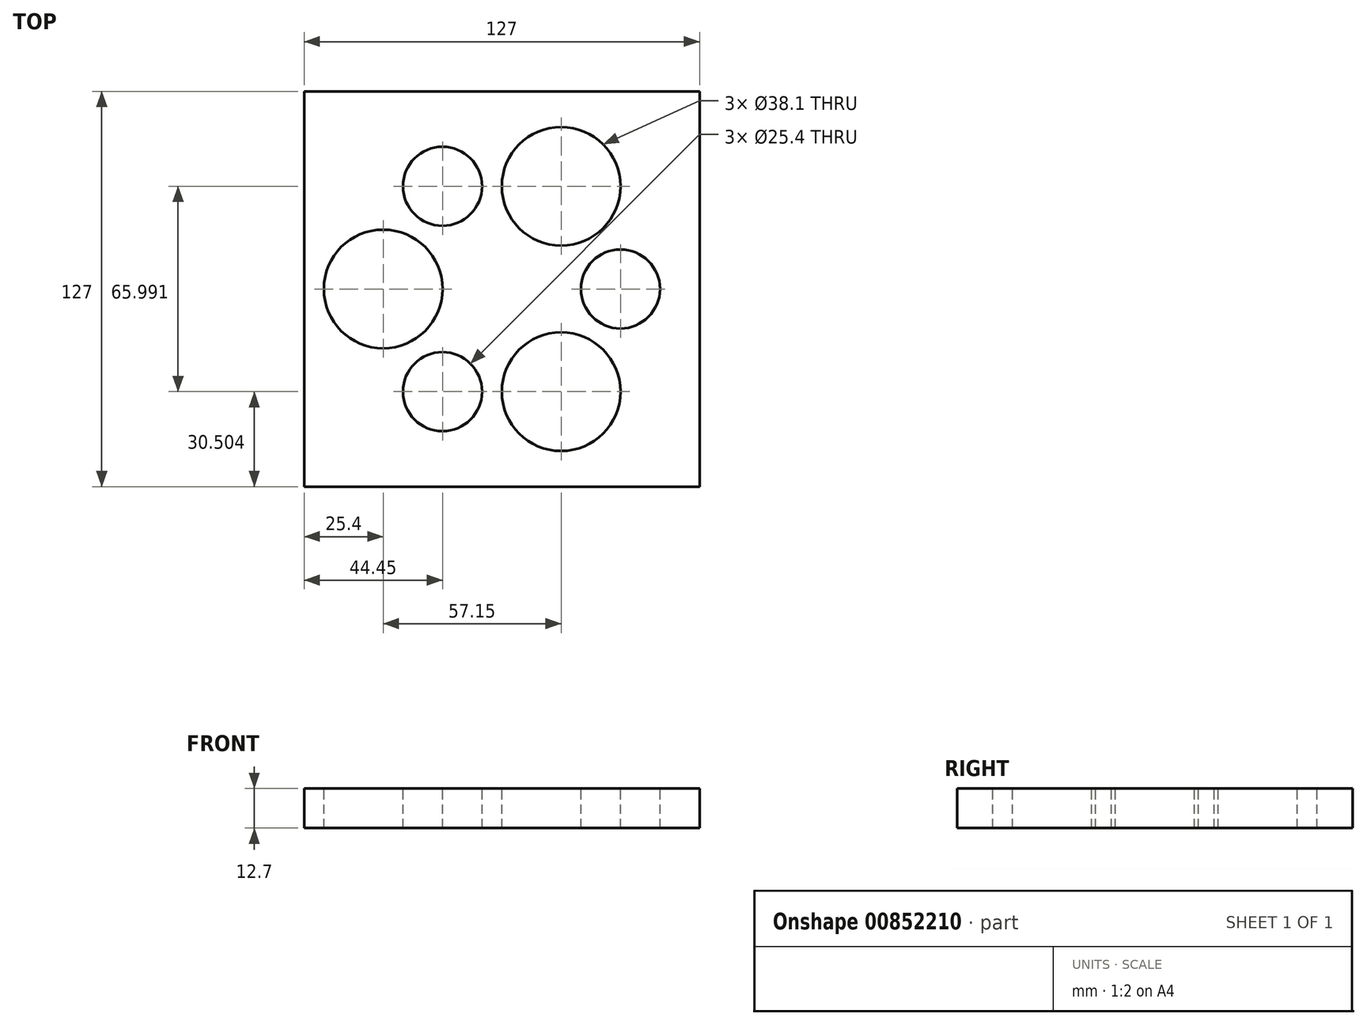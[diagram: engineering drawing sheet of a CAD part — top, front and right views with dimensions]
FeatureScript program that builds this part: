
annotation { "Feature Type Name" : "Feature", "Feature Type Description" : "" }
export const myFeature = defineFeature(function(context is Context, id is Id, definition is map)
    precondition{}
    {
        {
            var Q0;
            Q0=qCreatedBy(makeId("Top.planeOp"),FACE);
            var sketch = newSketch(context, id + "F0", { "sketchPlane" : qUnion([Q0])});
            skLineSegment(sketch, "E0.bottom", {"start": v(0, 0) * mm, "end": v(127, 0) * mm});
            skLineSegment(sketch, "E0.top", {"start": v(0, 127) * mm, "end": v(127, 127) * mm});
            skLineSegment(sketch, "E0.left", {"start": v(0, 0) * mm, "end": v(0, 127) * mm});
            skLineSegment(sketch, "E0.right", {"start": v(127, 0) * mm, "end": v(127, 127) * mm});
            skLineSegment(sketch, "E1", {"start": v(0, 127) * mm, "end": v(127, 0) * mm, "construction": true});
            skLineSegment(sketch, "E2", {"start": v(127, 127) * mm, "end": v(0, 0) * mm, "construction": true});
            skCircle(sketch, "E3.cCircle", {"center": v(63.5, 63.5) * mm, "radius": 33 * mm, "construction": true});
            skLineSegment(sketch, "E3.0", {"start": v(44.45, 96.5) * mm, "end": v(82.55, 96.5) * mm, "construction": true});
            skLineSegment(sketch, "E3.1", {"start": v(82.55, 96.5) * mm, "end": v(101.6, 63.5) * mm, "construction": true});
            skLineSegment(sketch, "E3.2", {"start": v(101.6, 63.5) * mm, "end": v(82.55, 30.5) * mm, "construction": true});
            skLineSegment(sketch, "E3.3", {"start": v(82.55, 30.5) * mm, "end": v(44.45, 30.5) * mm, "construction": true});
            skLineSegment(sketch, "E3.4", {"start": v(44.45, 30.5) * mm, "end": v(25.4, 63.5) * mm, "construction": true});
            skLineSegment(sketch, "E3.5", {"start": v(25.4, 63.5) * mm, "end": v(44.45, 96.5) * mm, "construction": true});
            skPoint(sketch, "E3.0.midPoint", {"position": v(63.5, 96.5) * mm});
            skCircle(sketch, "E4", {"center": v(44.45, 96.5) * mm, "radius": 12.7 * mm, "construction": true});
            skCircle(sketch, "E5", {"center": v(44.45, 96.5) * mm, "radius": 19.05 * mm, "construction": true});
            skCircle(sketch, "E6", {"center": v(82.55, 96.5) * mm, "radius": 12.7 * mm, "construction": true});
            skCircle(sketch, "E7", {"center": v(82.55, 96.5) * mm, "radius": 19.05 * mm, "construction": true});
            skCircle(sketch, "E8", {"center": v(101.6, 63.5) * mm, "radius": 12.7 * mm, "construction": true});
            skCircle(sketch, "E9", {"center": v(101.6, 63.5) * mm, "radius": 19.05 * mm, "construction": true});
            skCircle(sketch, "E10", {"center": v(82.55, 30.5) * mm, "radius": 12.7 * mm, "construction": true});
            skCircle(sketch, "E11", {"center": v(82.55, 30.5) * mm, "radius": 19.05 * mm, "construction": true});
            skCircle(sketch, "E12", {"center": v(44.45, 30.5) * mm, "radius": 12.7 * mm, "construction": true});
            skCircle(sketch, "E13", {"center": v(44.45, 30.5) * mm, "radius": 19.05 * mm, "construction": true});
            skCircle(sketch, "E14", {"center": v(25.4, 63.5) * mm, "radius": 12.7 * mm, "construction": true});
            skCircle(sketch, "E15", {"center": v(25.4, 63.5) * mm, "radius": 19.05 * mm, "construction": true});
            skSolve(sketch);
        }
        {
            var Q0;
            Q0=makeQuery(id+"F0.imprint","IMPRINT",FACE,{"disambiguationData":[TD([[makeQuery(id+"F0.imprint","IMPRINT",EDGE,{"derivedFrom":sQuery(id+"F0.wireOp",EDGE,"E0.bottom")}),1.0]])]});
            extrude(context, id + "F1", {"entities" : qUnion([Q0]), "depth" : 12.7 * mm, "offsetDistance" : 25.4 * mm});
        }
        {
            var Q0;
            Q0=makeQuery(id+"F1.opExtrude","CAP_FACE",FACE,{"disambiguationData":[OSD([sQuery(id+"F0.wireOp",EDGE,"E0.bottom"),sQuery(id+"F0.wireOp",EDGE,"E0.top"),sQuery(id+"F0.wireOp",EDGE,"E0.left"),sQuery(id+"F0.wireOp",EDGE,"E0.right")])],"isStart":false});
            var sketch = newSketch(context, id + "F2", { "sketchPlane" : qUnion([Q0])});
            skLineSegment(sketch, "E16.bottom", {"start": v(0, 0) * mm, "end": v(127, 0) * mm});
            skLineSegment(sketch, "E16.top", {"start": v(0, 127) * mm, "end": v(127, 127) * mm});
            skLineSegment(sketch, "E16.left", {"start": v(0, 0) * mm, "end": v(0, 127) * mm});
            skLineSegment(sketch, "E16.right", {"start": v(127, 0) * mm, "end": v(127, 127) * mm});
            skLineSegment(sketch, "E17", {"start": v(0, 127) * mm, "end": v(127, 0) * mm, "construction": true});
            skLineSegment(sketch, "E18", {"start": v(127, 127) * mm, "end": v(0, 0) * mm, "construction": true});
            skCircle(sketch, "E19.cCircle", {"center": v(63.5, 63.5) * mm, "radius": 33 * mm, "construction": true});
            skLineSegment(sketch, "E19.0", {"start": v(44.45, 96.5) * mm, "end": v(82.55, 96.5) * mm, "construction": true});
            skLineSegment(sketch, "E19.1", {"start": v(82.55, 96.5) * mm, "end": v(101.6, 63.5) * mm, "construction": true});
            skLineSegment(sketch, "E19.2", {"start": v(101.6, 63.5) * mm, "end": v(82.55, 30.5) * mm, "construction": true});
            skLineSegment(sketch, "E19.3", {"start": v(82.55, 30.5) * mm, "end": v(44.45, 30.5) * mm, "construction": true});
            skLineSegment(sketch, "E19.4", {"start": v(44.45, 30.5) * mm, "end": v(25.4, 63.5) * mm, "construction": true});
            skLineSegment(sketch, "E19.5", {"start": v(25.4, 63.5) * mm, "end": v(44.45, 96.5) * mm, "construction": true});
            skPoint(sketch, "E19.0.midPoint", {"position": v(63.5, 96.5) * mm});
            skCircle(sketch, "E20", {"center": v(44.45, 96.5) * mm, "radius": 12.7 * mm});
            skCircle(sketch, "E21", {"center": v(44.45, 96.5) * mm, "radius": 19.05 * mm, "construction": true});
            skCircle(sketch, "E22", {"center": v(82.55, 96.5) * mm, "radius": 12.7 * mm, "construction": true});
            skCircle(sketch, "E23", {"center": v(82.55, 96.5) * mm, "radius": 19.05 * mm});
            skCircle(sketch, "E24", {"center": v(101.6, 63.5) * mm, "radius": 12.7 * mm});
            skCircle(sketch, "E25", {"center": v(101.6, 63.5) * mm, "radius": 19.05 * mm, "construction": true});
            skCircle(sketch, "E26", {"center": v(82.55, 30.5) * mm, "radius": 12.7 * mm, "construction": true});
            skCircle(sketch, "E27", {"center": v(82.55, 30.5) * mm, "radius": 19.05 * mm});
            skCircle(sketch, "E28", {"center": v(44.45, 30.5) * mm, "radius": 12.7 * mm});
            skCircle(sketch, "E29", {"center": v(44.45, 30.5) * mm, "radius": 19.05 * mm, "construction": true});
            skCircle(sketch, "E30", {"center": v(25.4, 63.5) * mm, "radius": 12.7 * mm, "construction": true});
            skCircle(sketch, "E31", {"center": v(25.4, 63.5) * mm, "radius": 19.05 * mm});
            skSolve(sketch);
        }
        {
            var Q0;
            Q0=makeQuery(id+"F2.imprint","IMPRINT",FACE,{"disambiguationData":[TD([[makeQuery(id+"F2.imprint","IMPRINT",EDGE,{"derivedFrom":sQuery(id+"F2.wireOp",EDGE,"E23")}),1.0]])]});
            var Q1;
            Q1=makeQuery(id+"F2.imprint","IMPRINT",FACE,{"disambiguationData":[TD([[makeQuery(id+"F2.imprint","IMPRINT",EDGE,{"derivedFrom":sQuery(id+"F2.wireOp",EDGE,"E20")}),1.0]])]});
            var Q2;
            Q2=makeQuery(id+"F2.imprint","IMPRINT",FACE,{"disambiguationData":[TD([[makeQuery(id+"F2.imprint","IMPRINT",EDGE,{"derivedFrom":sQuery(id+"F2.wireOp",EDGE,"E31")}),1.0]])]});
            var Q3;
            Q3=makeQuery(id+"F2.imprint","IMPRINT",FACE,{"disambiguationData":[TD([[makeQuery(id+"F2.imprint","IMPRINT",EDGE,{"derivedFrom":sQuery(id+"F2.wireOp",EDGE,"E28")}),1.0]])]});
            var Q4;
            Q4=makeQuery(id+"F2.imprint","IMPRINT",FACE,{"disambiguationData":[TD([[makeQuery(id+"F2.imprint","IMPRINT",EDGE,{"derivedFrom":sQuery(id+"F2.wireOp",EDGE,"E27")}),1.0]])]});
            var Q5;
            Q5=makeQuery(id+"F2.imprint","IMPRINT",FACE,{"disambiguationData":[TD([[makeQuery(id+"F2.imprint","IMPRINT",EDGE,{"derivedFrom":sQuery(id+"F2.wireOp",EDGE,"E24")}),1.0]])]});
            var Q6;
            Q6=sQuery(id+"F2.wireOp",EDGE,"E20");
            var Q7;
            Q7=sQuery(id+"F2.wireOp",EDGE,"E23");
            var Q8;
            Q8=sQuery(id+"F2.wireOp",EDGE,"E24");
            var Q9;
            Q9=sQuery(id+"F2.wireOp",EDGE,"E27");
            var Q10;
            Q10=sQuery(id+"F2.wireOp",EDGE,"E28");
            var Q11;
            Q11=sQuery(id+"F2.wireOp",EDGE,"E31");
            extrude(context, id + "F3", {"entities" : qUnion([Q0, Q1, Q2, Q3, Q4, Q5]), "operationType" : NewBodyOperationType.REMOVE, "surfaceEntities" : qUnion([Q6, Q7, Q8, Q9, Q10, Q11]), "depth" : -25.4 * mm, "offsetDistance" : 25.4 * mm});
        }
    });
